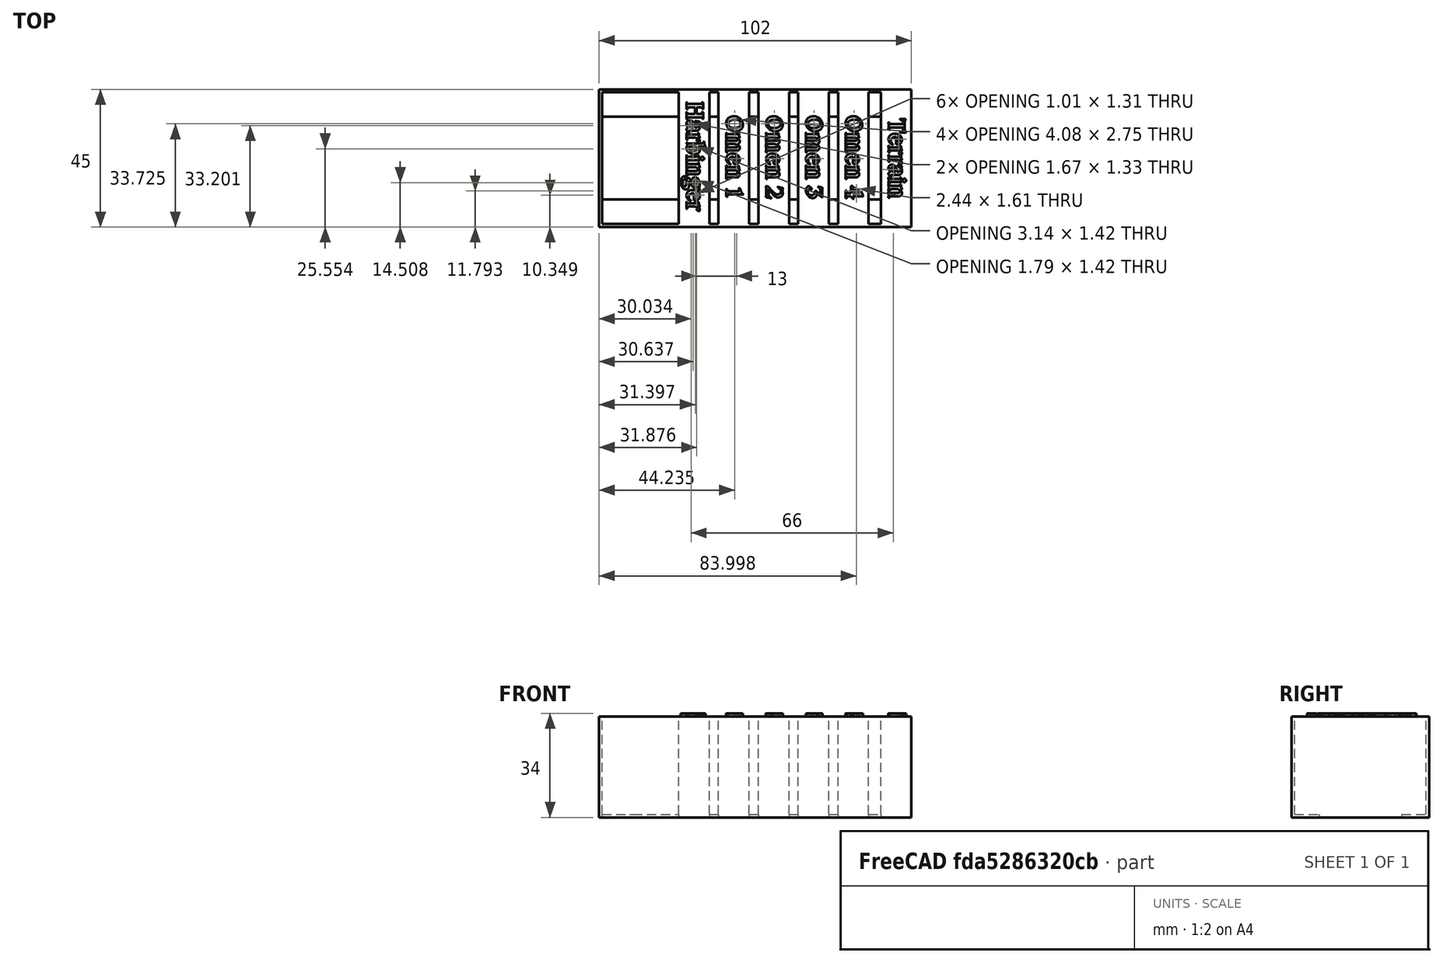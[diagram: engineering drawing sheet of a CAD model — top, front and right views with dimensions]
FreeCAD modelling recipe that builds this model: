
FCSTD DOCUMENT  (FreeCAD 0.18R4 (GitTag))
Label: harbringer
License: All rights reserved
LicenseURL: http://en.wikipedia.org/wiki/All_rights_reserved
objects: Part::Box×12, Part::Part2DObjectPython×6, Part::Extrusion×6, Part::Cut×3, Part::MultiFuse×3
note: 30 computed .brp shape members not serialized (recipe doc carries the construction recipe); baked Part::Feature solids carry a one-line shape summary decoded from their .brp

FEATURE [Part::Box] Box  label="Cube"
  AttacherType = Attacher::AttachEngine3D
  Height = 33
  Length = 202
  Placement = pos=(0,-1,0) rot=(0,0,1;0rad)
  Width = 45
FEATURE [Part::Box] Box001  label="Cube001"
  AttacherType = Attacher::AttachEngine3D
  Height = 33
  Length = 200
  Placement = pos=(1,0,0) rot=(0,0,1;0rad)
  Width = 43
FEATURE [Part::Cut] Cut
  Base = -> Box
  Tool = -> Box001
FEATURE [Part::Box] Box002  label="Cube002"
  AttacherType = Attacher::AttachEngine3D
  Height = 1
  Length = 202
  Width = 8
FEATURE [Part::Box] Box003  label="Cube003"
  AttacherType = Attacher::AttachEngine3D
  Height = 1
  Length = 202
  Placement = pos=(0,35,0) rot=(0,0,1;0rad)
  Width = 8
FEATURE [Part::MultiFuse] Fusion
  Shapes = -> [Cut,Box002,Box003]
FEATURE [Part::Box] Box004  label="Cube004"
  AttacherType = Attacher::AttachEngine3D
  Height = 33
  Length = 10
  Placement = pos=(26,0,0) rot=(0,0,1;0rad)
  Width = 43
FEATURE [Part::Box] Box005  label="Cube005"
  AttacherType = Attacher::AttachEngine3D
  Height = 33
  Length = 10
  Placement = pos=(39,0,0) rot=(0,0,1;0rad)
  Width = 43
FEATURE [Part::Box] Box006  label="Cube006"
  AttacherType = Attacher::AttachEngine3D
  Height = 33
  Length = 10
  Placement = pos=(52,0,0) rot=(0,0,1;0rad)
  Width = 43
FEATURE [Part::Box] Box007  label="Cube007"
  AttacherType = Attacher::AttachEngine3D
  Height = 33
  Length = 10
  Placement = pos=(65,0,0) rot=(0,0,1;0rad)
  Width = 43
FEATURE [Part::Box] Box008  label="Cube008"
  AttacherType = Attacher::AttachEngine3D
  Height = 33
  Length = 10
  Placement = pos=(78,0,0) rot=(0,0,1;0rad)
  Width = 43
FEATURE [Part::Box] Box009  label="Cube009"
  AttacherType = Attacher::AttachEngine3D
  Height = 33
  Length = 10
  Placement = pos=(92,0,0) rot=(0,0,1;0rad)
  Width = 43
FEATURE [Part::Box] Box010  label="Cube010"
  AttacherType = Attacher::AttachEngine3D
  Height = 33
  Length = 121
  Placement = pos=(102,-1,0) rot=(0,0,1;0rad)
  Width = 45
FEATURE [Part::MultiFuse] Fusion001
  Shapes = -> [Fusion,Box005,Box006,Box007,Box009,Box004,Box008]
FEATURE [Part::Cut] Cut001
  Base = -> Fusion001
  Tool = -> Box010
FEATURE [Part::Box] Box015  label="Cube015"
  AttacherType = Attacher::AttachEngine3D
  Height = 32
  Length = 1
  Placement = pos=(10,0,1) rot=(0,0,1;0rad)
  Width = 43
FEATURE [Part::Part2DObjectPython] ShapeString  # Draft 2D object (typed FeaturePython)
  FontFile = <userpath>/Downloads/talisman/Caxton Bold.otf
  Placement = pos=(-37.35,46.93,33) rot=(0,0,-1;1.5708rad)
  Size = 3
  String = Harbinger
  Tracking = 0
FEATURE [Part::Part2DObjectPython] ShapeString004  # Draft 2D object (typed FeaturePython)
  FontFile = <userpath>/Downloads/talisman/Caxton Bold.otf
  Placement = pos=(33.65,41.43,33) rot=(0,0,-1;1.5708rad)
  Size = 3
  String = Terrain
  Tracking = 0
FEATURE [Part::Part2DObjectPython] ShapeString005  # Draft 2D object (typed FeaturePython)
  FontFile = <userpath>/Downloads/talisman/Caxton Bold.otf
  Placement = pos=(-23.35,42.43,33) rot=(0,0,-1;1.5708rad)
  Size = 3
  String = Omen 1
  Tracking = 0
FEATURE [Part::Part2DObjectPython] ShapeString006  # Draft 2D object (typed FeaturePython)
  FontFile = <userpath>/Downloads/talisman/Caxton Bold.otf
  Placement = pos=(-9.35,42.43,33) rot=(0,0,-1;1.5708rad)
  Size = 3
  String = Omen 2
  Tracking = 0
FEATURE [Part::Part2DObjectPython] ShapeString007  # Draft 2D object (typed FeaturePython)
  FontFile = <userpath>/Downloads/talisman/Caxton Bold.otf
  Placement = pos=(4.65,42.43,33) rot=(0,0,-1;1.5708rad)
  Size = 3
  String = Omen 3
  Tracking = 0
FEATURE [Part::Part2DObjectPython] ShapeString008  # Draft 2D object (typed FeaturePython)
  FontFile = <userpath>/Downloads/talisman/Caxton Bold.otf
  Placement = pos=(18.65,42.43,33) rot=(0,0,-1;1.5708rad)
  Size = 3
  String = Omen 4
  Tracking = 0
FEATURE [Part::Extrusion] Extrude
  Base = -> ShapeString
  Dir = (0,0,1)
  DirMode = 2
  FaceMakerClass = Part::FaceMakerBullseye
  LengthFwd = 1
  LengthRev = 0
  Placement = pos=(66,-7,0) rot=(0,0,1;0rad)
  Solid = false
  Symmetric = false
FEATURE [Part::Extrusion] Extrude001
  Base = -> ShapeString004
  Dir = (0,0,1)
  DirMode = 2
  FaceMakerClass = Part::FaceMakerBullseye
  LengthFwd = 1
  LengthRev = 0
  Placement = pos=(61,-7,0) rot=(0,0,1;0rad)
  Solid = false
  Symmetric = false
FEATURE [Part::Extrusion] Extrude002
  Base = -> ShapeString005
  Dir = (0,0,1)
  DirMode = 2
  FaceMakerClass = Part::FaceMakerBullseye
  LengthFwd = 1
  LengthRev = 0
  Placement = pos=(65,-7,0) rot=(0,0,1;0rad)
  Solid = false
  Symmetric = false
FEATURE [Part::Extrusion] Extrude003
  Base = -> ShapeString006
  Dir = (0,0,1)
  DirMode = 2
  FaceMakerClass = Part::FaceMakerBullseye
  LengthFwd = 1
  LengthRev = 0
  Placement = pos=(64,-7,0) rot=(0,0,1;0rad)
  Solid = false
  Symmetric = false
FEATURE [Part::Extrusion] Extrude004
  Base = -> ShapeString007
  Dir = (0,0,1)
  DirMode = 2
  FaceMakerClass = Part::FaceMakerBullseye
  LengthFwd = 1
  LengthRev = 0
  Placement = pos=(63,-7,0) rot=(0,0,1;0rad)
  Solid = false
  Symmetric = false
FEATURE [Part::Extrusion] Extrude005
  Base = -> ShapeString008
  Dir = (0,0,1)
  DirMode = 2
  FaceMakerClass = Part::FaceMakerBullseye
  LengthFwd = 1
  LengthRev = 0
  Placement = pos=(62,-7,0) rot=(0,0,1;0rad)
  Solid = false
  Symmetric = false
FEATURE [Part::Cut] Cut002
  Base = -> Cut001
  Tool = -> Box015
FEATURE [Part::MultiFuse] Fusion002
  Shapes = -> [Extrude005,Extrude,Extrude001,Extrude003,Extrude004,Extrude002]
